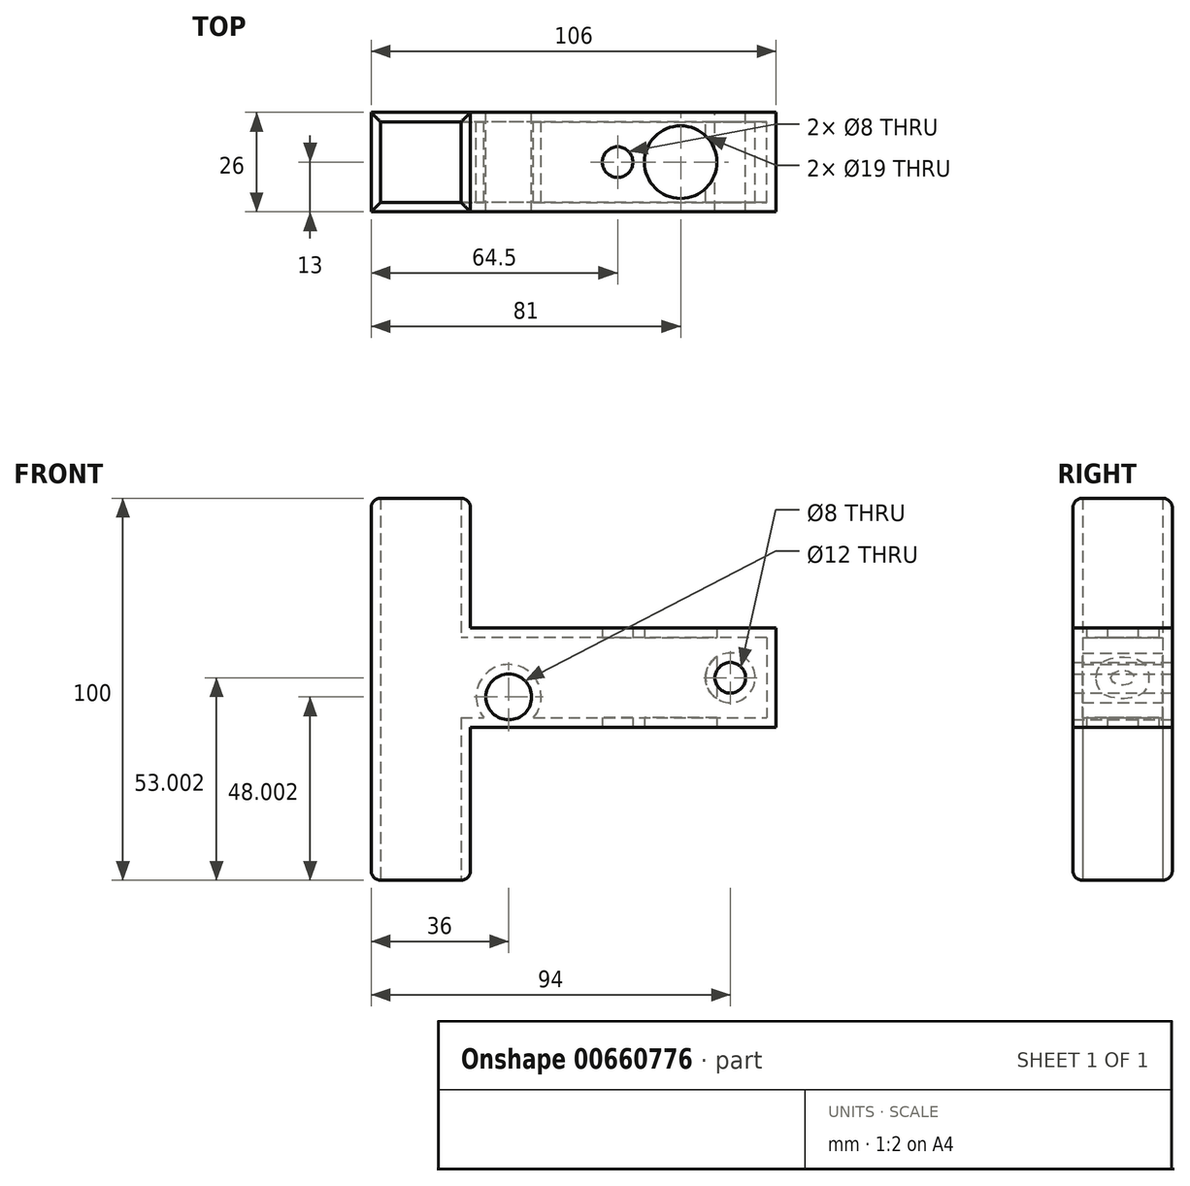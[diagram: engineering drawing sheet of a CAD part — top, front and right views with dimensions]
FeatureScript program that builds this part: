
annotation { "Feature Type Name" : "Feature", "Feature Type Description" : "" }
export const myFeature = defineFeature(function(context is Context, id is Id, definition is map)
    precondition{}
    {
        {
            var Q0;
            Q0=qCreatedBy(makeId("Front.planeOp"),FACE);
            var sketch = newSketch(context, id + "F0", { "sketchPlane" : qUnion([Q0])});
            skLineSegment(sketch, "E0.bottom", {"start": v(0, 60) * mm, "end": v(-26, 60) * mm});
            skLineSegment(sketch, "E0.top", {"start": v(0, -40) * mm, "end": v(-26, -40) * mm});
            skLineSegment(sketch, "E0.left", {"start": v(0, 60) * mm, "end": v(0, -40) * mm});
            skLineSegment(sketch, "E0.right", {"start": v(-26, 60) * mm, "end": v(-26, -40) * mm});
            skLineSegment(sketch, "E1.top", {"start": v(0, 0) * mm, "end": v(80, 0) * mm});
            skLineSegment(sketch, "E1.right", {"start": v(80, 26) * mm, "end": v(80, 0) * mm});
            skLineSegment(sketch, "E2", {"start": v(80, 26) * mm, "end": v(0, 26) * mm});
            skCircle(sketch, "E3", {"center": v(10, 8) * mm, "radius": 6 * mm});
            skCircle(sketch, "E4", {"center": v(68, 13) * mm, "radius": 4 * mm});
            skSolve(sketch);
        }
        {
            var Q0;
            {var subQ3=sQuery(id+"F0.wireOp",EDGE,"E0.bottom");Q0=makeQuery(id+"F0.imprint","IMPRINT",FACE,{"disambiguationData":[TD([[makeQuery(id+"F0.imprint","IMPRINT",EDGE,{"derivedFrom":subQ3}),1.0]])]});}
            var Q1;
            {var subQ0=sQuery(id+"F0.wireOp",EDGE,"E1.top");Q1=makeQuery(id+"F0.imprint","IMPRINT",FACE,{"disambiguationData":[TD([[makeQuery(id+"F0.imprint","IMPRINT",EDGE,{"derivedFrom":subQ0}),1.0]])]});}
            extrude(context, id + "F1", {"entities" : qUnion([Q0, Q1]), "endBound" : BoundingType.SYMMETRIC, "depth" : 26 * mm, "offsetDistance" : 25 * mm});
        }
        {
            var Q0;
            Q0=makeQuery(id+"F1.opExtrude","SWEPT_FACE",FACE,{"disambiguationData":[OSD([sQuery(id+"F0.wireOp",EDGE,"E0.bottom")])]});
            var Q1;
            Q1=makeQuery(id+"F1.opExtrude","SWEPT_FACE",FACE,{"disambiguationData":[OSD([sQuery(id+"F0.wireOp",EDGE,"E0.top")])]});
            var Q2;
            Q2=makeQuery(id+"F1.opExtrude","SWEPT_BODY",BODY,{"disambiguationData":[OSD([sQuery(id+"F0.wireOp",EDGE,"E0.bottom"),sQuery(id+"F0.wireOp",EDGE,"E0.top"),sQuery(id+"F0.wireOp",EDGE,"E0.left"),sQuery(id+"F0.wireOp",EDGE,"E0.right"),sQuery(id+"F0.wireOp",EDGE,"E1.top"),sQuery(id+"F0.wireOp",EDGE,"E1.right"),sQuery(id+"F0.wireOp",EDGE,"E2"),sQuery(id+"F0.wireOp",EDGE,"E3"),sQuery(id+"F0.wireOp",EDGE,"E4")])]});
            shell(context, id + "F2", {"entities" : qUnion([Q0, Q1]), "parts" : qUnion([Q2]), "thickness" : 2.5 * mm});
        }
        {
            var Q0;
            Q0=qCreatedBy(makeId("Top.planeOp"),FACE);
            var sketch = newSketch(context, id + "F3", { "sketchPlane" : qUnion([Q0])});
            skCircle(sketch, "E5", {"center": v(55, 0) * mm, "radius": 9.5 * mm});
            skCircle(sketch, "E6", {"center": v(38.5, 0) * mm, "radius": 4 * mm});
            skSolve(sketch);
        }
        {
            var Q0;
            Q0=makeQuery(id+"F3.imprint","IMPRINT",FACE,{"disambiguationData":[TD([[makeQuery(id+"F3.imprint","IMPRINT",EDGE,{"derivedFrom":sQuery(id+"F3.wireOp",EDGE,"E5")}),1.0]])]});
            var Q1;
            Q1=makeQuery(id+"F3.imprint","IMPRINT",FACE,{"disambiguationData":[TD([[makeQuery(id+"F3.imprint","IMPRINT",EDGE,{"derivedFrom":sQuery(id+"F3.wireOp",EDGE,"E6")}),1.0]])]});
            extrude(context, id + "F4", {"entities" : qUnion([Q0, Q1]), "operationType" : NewBodyOperationType.REMOVE, "endBound" : BoundingType.SYMMETRIC, "depth" : 100 * mm, "offsetDistance" : 25 * mm});
        }
        {
            var Q0;
            Q0=makeQuery(id+"F1.opExtrude","SWEPT_EDGE",EDGE,{"disambiguationData":[OSD([sQuery(id+"F0.wireOp",EDGE,"E0.bottom"),sQuery(id+"F0.wireOp",EDGE,"E0.left")])]});
            var Q1;
            Q1=makeQuery(id+"F1.opExtrude","CAP_EDGE",EDGE,{"disambiguationData":[OSD([sQuery(id+"F0.wireOp",EDGE,"E0.bottom")])],"isStart":false});
            var Q2;
            Q2=makeQuery(id+"F1.opExtrude","CAP_EDGE",EDGE,{"disambiguationData":[OSD([sQuery(id+"F0.wireOp",EDGE,"E0.bottom")])],"isStart":true});
            var Q3;
            Q3=makeQuery(id+"F1.opExtrude","SWEPT_EDGE",EDGE,{"disambiguationData":[OSD([sQuery(id+"F0.wireOp",EDGE,"E0.bottom"),sQuery(id+"F0.wireOp",EDGE,"E0.right")])]});
            var Q4;
            Q4=makeQuery(id+"F1.opExtrude","SWEPT_EDGE",EDGE,{"disambiguationData":[OSD([sQuery(id+"F0.wireOp",EDGE,"E0.top"),sQuery(id+"F0.wireOp",EDGE,"E0.right")])]});
            var Q5;
            Q5=makeQuery(id+"F1.opExtrude","CAP_EDGE",EDGE,{"disambiguationData":[OSD([sQuery(id+"F0.wireOp",EDGE,"E0.top")])],"isStart":true});
            var Q6;
            Q6=makeQuery(id+"F1.opExtrude","SWEPT_EDGE",EDGE,{"disambiguationData":[OSD([sQuery(id+"F0.wireOp",EDGE,"E0.top"),sQuery(id+"F0.wireOp",EDGE,"E0.left")])]});
            var Q7;
            Q7=makeQuery(id+"F1.opExtrude","CAP_EDGE",EDGE,{"disambiguationData":[OSD([sQuery(id+"F0.wireOp",EDGE,"E0.top")])],"isStart":false});
            fillet(context, id + "F5", {"entities" : qUnion([Q0, Q1, Q2, Q3, Q4, Q5, Q6, Q7]), "radius" : 2.5 * mm, "tangentPropagation" : true, "allowEdgeOverflow" : false});
        }
    });
